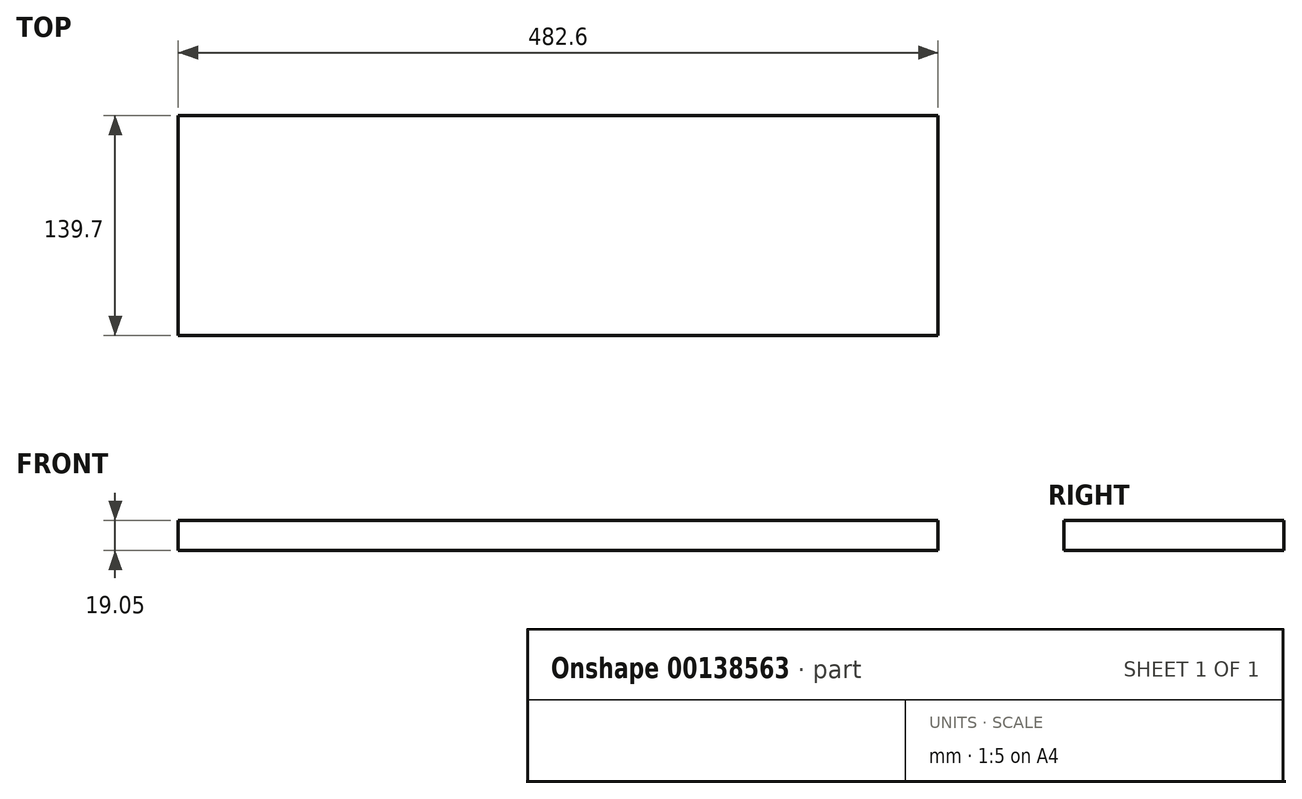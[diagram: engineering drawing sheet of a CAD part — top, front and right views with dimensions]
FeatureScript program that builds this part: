
annotation { "Feature Type Name" : "Feature", "Feature Type Description" : "" }
export const myFeature = defineFeature(function(context is Context, id is Id, definition is map)
    precondition{}
    {
        {
            var Q0;
            Q0=qCreatedBy(makeId("Top.planeOp"),FACE);
            var sketch = newSketch(context, id + "F0", { "sketchPlane" : qUnion([Q0])});
            skLineSegment(sketch, "E0.bottom", {"start": v(-241.3, 69.85) * mm, "end": v(241.3, 69.85) * mm});
            skLineSegment(sketch, "E0.top", {"start": v(-241.3, -69.85) * mm, "end": v(241.3, -69.85) * mm});
            skLineSegment(sketch, "E0.left", {"start": v(-241.3, 69.85) * mm, "end": v(-241.3, -69.85) * mm});
            skLineSegment(sketch, "E0.right", {"start": v(241.3, 69.85) * mm, "end": v(241.3, -69.85) * mm});
            skPoint(sketch, "E0.middle", {"position": v(0, 0) * mm});
            skSolve(sketch);
        }
        {
            var Q0;
            Q0=makeQuery(id+"F0.imprint","IMPRINT",FACE,{"disambiguationData":[TD([[makeQuery(id+"F0.imprint","IMPRINT",EDGE,{"derivedFrom":sQuery(id+"F0.wireOp",EDGE,"E0.bottom")}),-1.0]])]});
            extrude(context, id + "F1", {"entities" : qUnion([Q0]), "depth" : 19.05 * mm});
        }
    });
